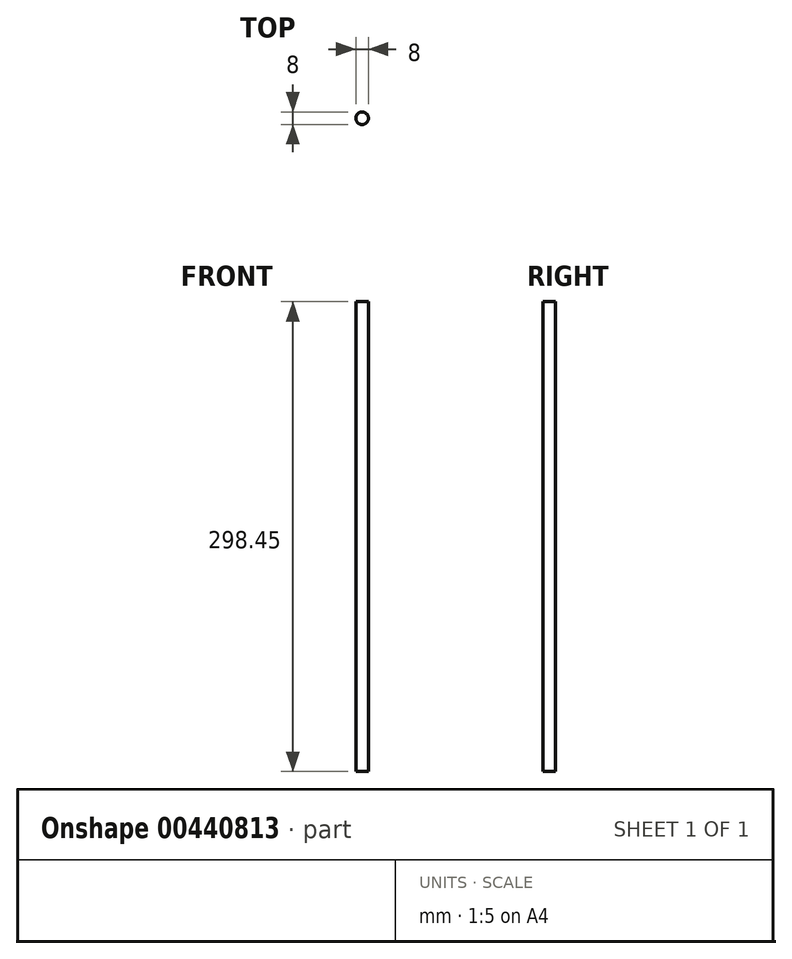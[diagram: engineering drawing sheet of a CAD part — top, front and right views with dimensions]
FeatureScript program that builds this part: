
annotation { "Feature Type Name" : "Feature", "Feature Type Description" : "" }
export const myFeature = defineFeature(function(context is Context, id is Id, definition is map)
    precondition{}
    {
        {
            var Q0;
            Q0=qCreatedBy(makeId("Top.planeOp"),FACE);
            var sketch = newSketch(context, id + "F0", { "sketchPlane" : qUnion([Q0])});
            skCircle(sketch, "E0", {"center": v(0, 0) * mm, "radius": 4 * mm});
            skSolve(sketch);
        }
        {
            var Q0;
            Q0 = qSketchRegion(id + "F0", true);
            extrude(context, id + "F1", {"entities" : qUnion([Q0]), "depth" : 298.45 * mm});
        }
    });
